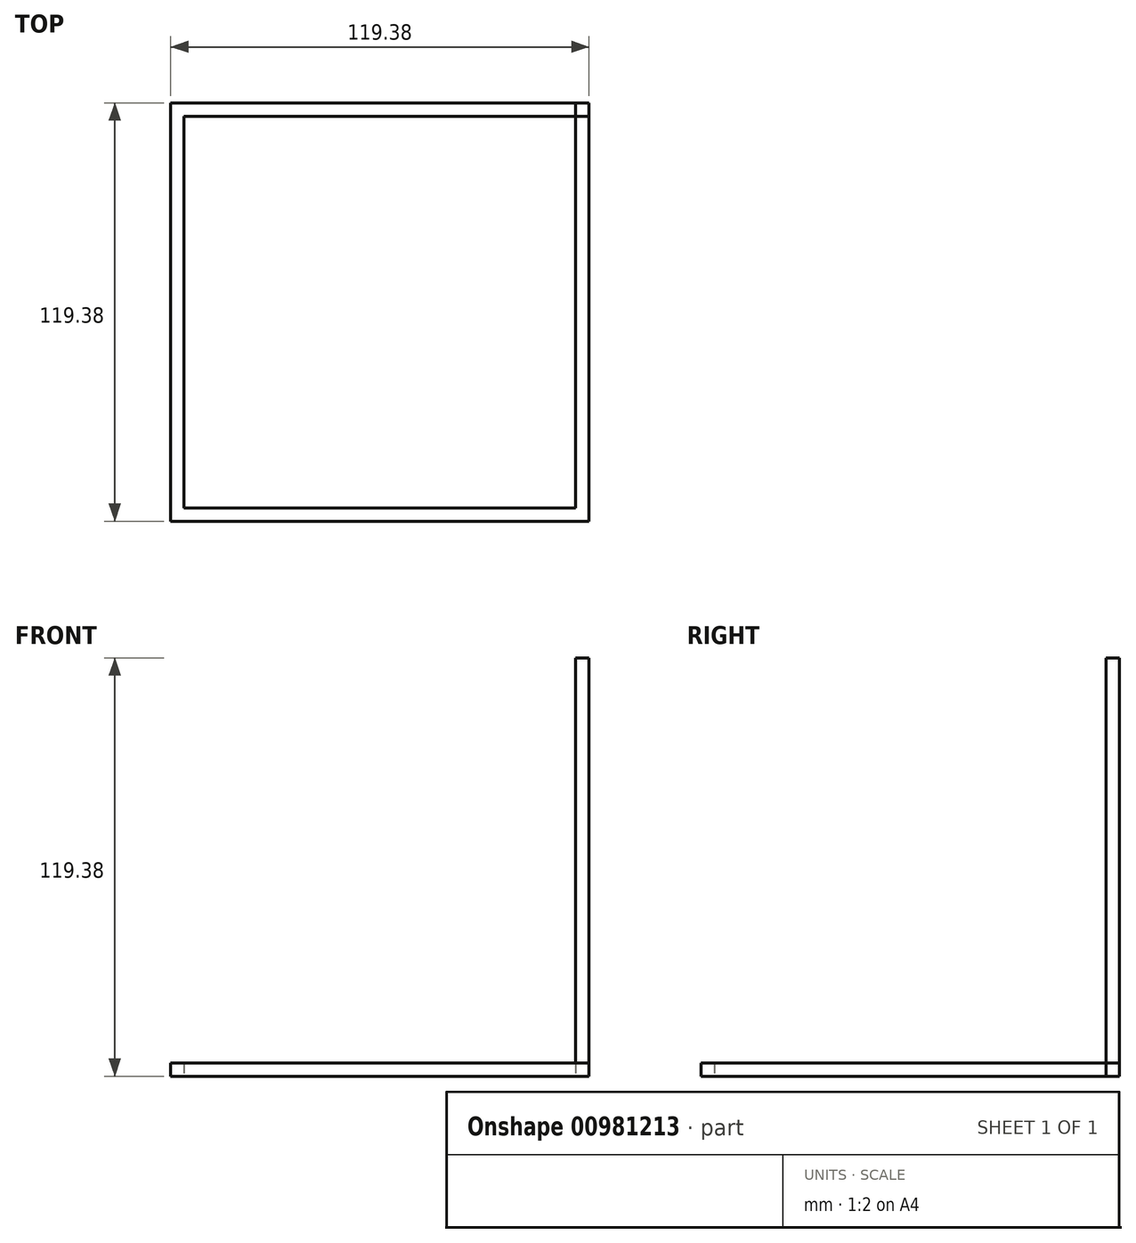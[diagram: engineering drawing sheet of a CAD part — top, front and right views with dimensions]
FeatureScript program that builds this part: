
annotation { "Feature Type Name" : "Feature", "Feature Type Description" : "" }
export const myFeature = defineFeature(function(context is Context, id is Id, definition is map)
    precondition{}
    {
        {
            var Q0;
            Q0=qCreatedBy(makeId("Top.planeOp"),FACE);
            var sketch = newSketch(context, id + "F0", { "sketchPlane" : qUnion([Q0])});
            skLineSegment(sketch, "E0.bottom", {"start": v(-55.16, 60.07) * mm, "end": v(64.22, 60.07) * mm});
            skLineSegment(sketch, "E0.top", {"start": v(-55.16, -59.31) * mm, "end": v(64.22, -59.31) * mm});
            skLineSegment(sketch, "E0.left", {"start": v(-55.16, 60.07) * mm, "end": v(-55.16, -59.31) * mm});
            skLineSegment(sketch, "E0.right", {"start": v(64.22, 60.07) * mm, "end": v(64.22, -59.31) * mm});
            skLineSegment(sketch, "E1.bottom", {"start": v(-51.35, 56.26) * mm, "end": v(60.4, 56.26) * mm});
            skLineSegment(sketch, "E1.top", {"start": v(-51.35, -55.5) * mm, "end": v(60.4, -55.5) * mm});
            skLineSegment(sketch, "E1.left", {"start": v(-51.35, 56.26) * mm, "end": v(-51.35, -55.5) * mm});
            skLineSegment(sketch, "E1.right", {"start": v(60.4, 56.26) * mm, "end": v(60.4, -55.5) * mm});
            skLineSegment(sketch, "E2.bottom", {"start": v(-55.16, 60.07) * mm, "end": v(-51.35, 60.07) * mm});
            skLineSegment(sketch, "E2.top", {"start": v(-55.16, 56.26) * mm, "end": v(-51.35, 56.26) * mm});
            skLineSegment(sketch, "E2.left", {"start": v(-55.16, 60.07) * mm, "end": v(-55.16, 56.26) * mm});
            skLineSegment(sketch, "E2.right", {"start": v(-51.35, 60.07) * mm, "end": v(-51.35, 56.26) * mm});
            skLineSegment(sketch, "E3.bottom", {"start": v(60.4, 56.26) * mm, "end": v(64.22, 56.26) * mm});
            skLineSegment(sketch, "E3.top", {"start": v(60.4, 60.07) * mm, "end": v(64.22, 60.07) * mm});
            skLineSegment(sketch, "E3.left", {"start": v(60.4, 56.26) * mm, "end": v(60.4, 60.07) * mm});
            skLineSegment(sketch, "E3.right", {"start": v(64.22, 56.26) * mm, "end": v(64.22, 60.07) * mm});
            skLineSegment(sketch, "E4.bottom", {"start": v(64.22, -59.31) * mm, "end": v(60.4, -59.31) * mm});
            skLineSegment(sketch, "E4.top", {"start": v(64.22, -55.5) * mm, "end": v(60.4, -55.5) * mm});
            skLineSegment(sketch, "E4.left", {"start": v(64.22, -59.31) * mm, "end": v(64.22, -55.5) * mm});
            skLineSegment(sketch, "E4.right", {"start": v(60.4, -59.31) * mm, "end": v(60.4, -55.5) * mm});
            skLineSegment(sketch, "E5.bottom", {"start": v(-55.16, -59.31) * mm, "end": v(-51.35, -59.31) * mm});
            skLineSegment(sketch, "E5.top", {"start": v(-55.16, -55.5) * mm, "end": v(-51.35, -55.5) * mm});
            skLineSegment(sketch, "E5.left", {"start": v(-55.16, -59.31) * mm, "end": v(-55.16, -55.5) * mm});
            skLineSegment(sketch, "E5.right", {"start": v(-51.35, -59.31) * mm, "end": v(-51.35, -55.5) * mm});
            skSolve(sketch);
        }
        {
            var Q0;
            Q0=makeQuery(id+"F0.imprint","IMPRINT",FACE,{"disambiguationData":[TD([[makeQuery(id+"F0.imprint","IMPRINT",EDGE,{"derivedFrom":sQuery(id+"F0.wireOp",EDGE,"E0.left")}),1.0]])]});
            var Q1;
            Q1=makeQuery(id+"F0.imprint","IMPRINT",FACE,{"disambiguationData":[TD([[makeQuery(id+"F0.imprint","IMPRINT",EDGE,{"derivedFrom":sQuery(id+"F0.wireOp",EDGE,"E0.bottom")}),-1.0]])]});
            var Q2;
            Q2=makeQuery(id+"F0.imprint","IMPRINT",FACE,{"disambiguationData":[TD([[makeQuery(id+"F0.imprint","IMPRINT",EDGE,{"derivedFrom":sQuery(id+"F0.wireOp",EDGE,"E0.right")}),-1.0]])]});
            var Q3;
            Q3=makeQuery(id+"F0.imprint","IMPRINT",FACE,{"disambiguationData":[TD([[makeQuery(id+"F0.imprint","IMPRINT",EDGE,{"derivedFrom":sQuery(id+"F0.wireOp",EDGE,"E0.top")}),1.0]])]});
            extrude(context, id + "F1", {"entities" : qUnion([Q0, Q1, Q2, Q3]), "depth" : 3.8 * mm, "offsetDistance" : 25.4 * mm});
        }
        {
            var Q0;
            Q0=makeQuery(id+"F0.imprint","IMPRINT",FACE,{"disambiguationData":[TD([[makeQuery(id+"F0.imprint","IMPRINT",EDGE,{"derivedFrom":sQuery(id+"F0.wireOp",EDGE,"E5.bottom")}),1.0]])]});
            var Q1;
            Q1=makeQuery(id+"F0.imprint","IMPRINT",FACE,{"disambiguationData":[TD([[makeQuery(id+"F0.imprint","IMPRINT",EDGE,{"derivedFrom":sQuery(id+"F0.wireOp",EDGE,"E4.bottom")}),-1.0]])]});
            var Q2;
            Q2=makeQuery(id+"F0.imprint","IMPRINT",FACE,{"disambiguationData":[TD([[makeQuery(id+"F0.imprint","IMPRINT",EDGE,{"derivedFrom":sQuery(id+"F0.wireOp",EDGE,"E3.bottom")}),1.0]])]});
            var Q3;
            Q3=makeQuery(id+"F0.imprint","IMPRINT",FACE,{"disambiguationData":[TD([[makeQuery(id+"F0.imprint","IMPRINT",EDGE,{"derivedFrom":sQuery(id+"F0.wireOp",EDGE,"E2.bottom")}),-1.0]])]});
            extrude(context, id + "F2", {"entities" : qUnion([Q0, Q1, Q2, Q3]), "depth" : 119.38 * mm, "offsetDistance" : 25.4 * mm});
        }
    });
